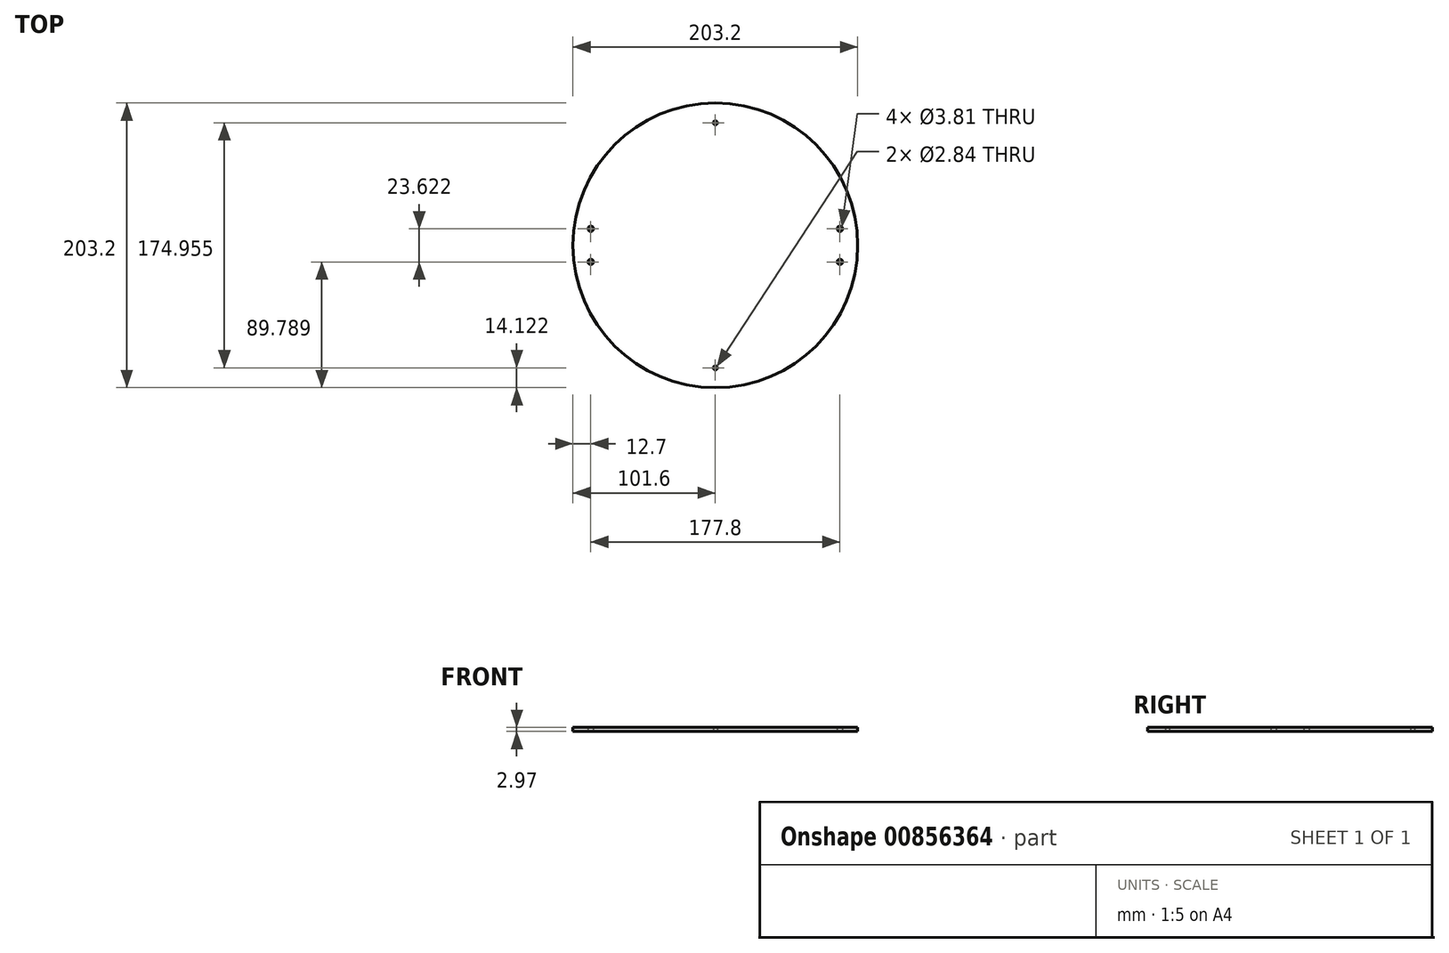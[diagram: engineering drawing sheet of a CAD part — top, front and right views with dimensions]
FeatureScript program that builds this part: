
annotation { "Feature Type Name" : "Feature", "Feature Type Description" : "" }
export const myFeature = defineFeature(function(context is Context, id is Id, definition is map)
    precondition{}
    {
        {
            var Q0;
            Q0=qCreatedBy(makeId("Top.planeOp"),FACE);
            var sketch = newSketch(context, id + "F0", { "sketchPlane" : qUnion([Q0])});
            skCircle(sketch, "E0", {"center": v(0, 0) * mm, "radius": 101.6 * mm});
            skCircle(sketch, "E1", {"center": v(-88.9, 11.81) * mm, "radius": 1.9 * mm});
            skCircle(sketch, "E2", {"center": v(0, 87.48) * mm, "radius": 1.42 * mm});
            skCircle(sketch, "E3", {"center": v(0, -87.48) * mm, "radius": 1.42 * mm});
            skCircle(sketch, "E4.MirrorC", {"center": v(-88.9, -11.81) * mm, "radius": 1.9 * mm});
            skCircle(sketch, "E5.MirrorC", {"center": v(88.9, 11.81) * mm, "radius": 1.9 * mm});
            skCircle(sketch, "E6.MirrorC", {"center": v(88.9, -11.81) * mm, "radius": 1.9 * mm});
            skSolve(sketch);
        }
        {
            var Q0;
            Q0=makeQuery(id+"F0.imprint","IMPRINT",FACE,{"disambiguationData":[TD([[makeQuery(id+"F0.imprint","IMPRINT",EDGE,{"derivedFrom":sQuery(id+"F0.wireOp",EDGE,"E0")}),1.0]])]});
            var Q1;
            Q1=sQuery(id+"F0.wireOp",EDGE,"E0");
            extrude(context, id + "F1", {"entities" : qUnion([Q0]), "surfaceEntities" : qUnion([Q1]), "depth" : 2.97 * mm, "offsetDistance" : 25.4 * mm});
        }
    });
